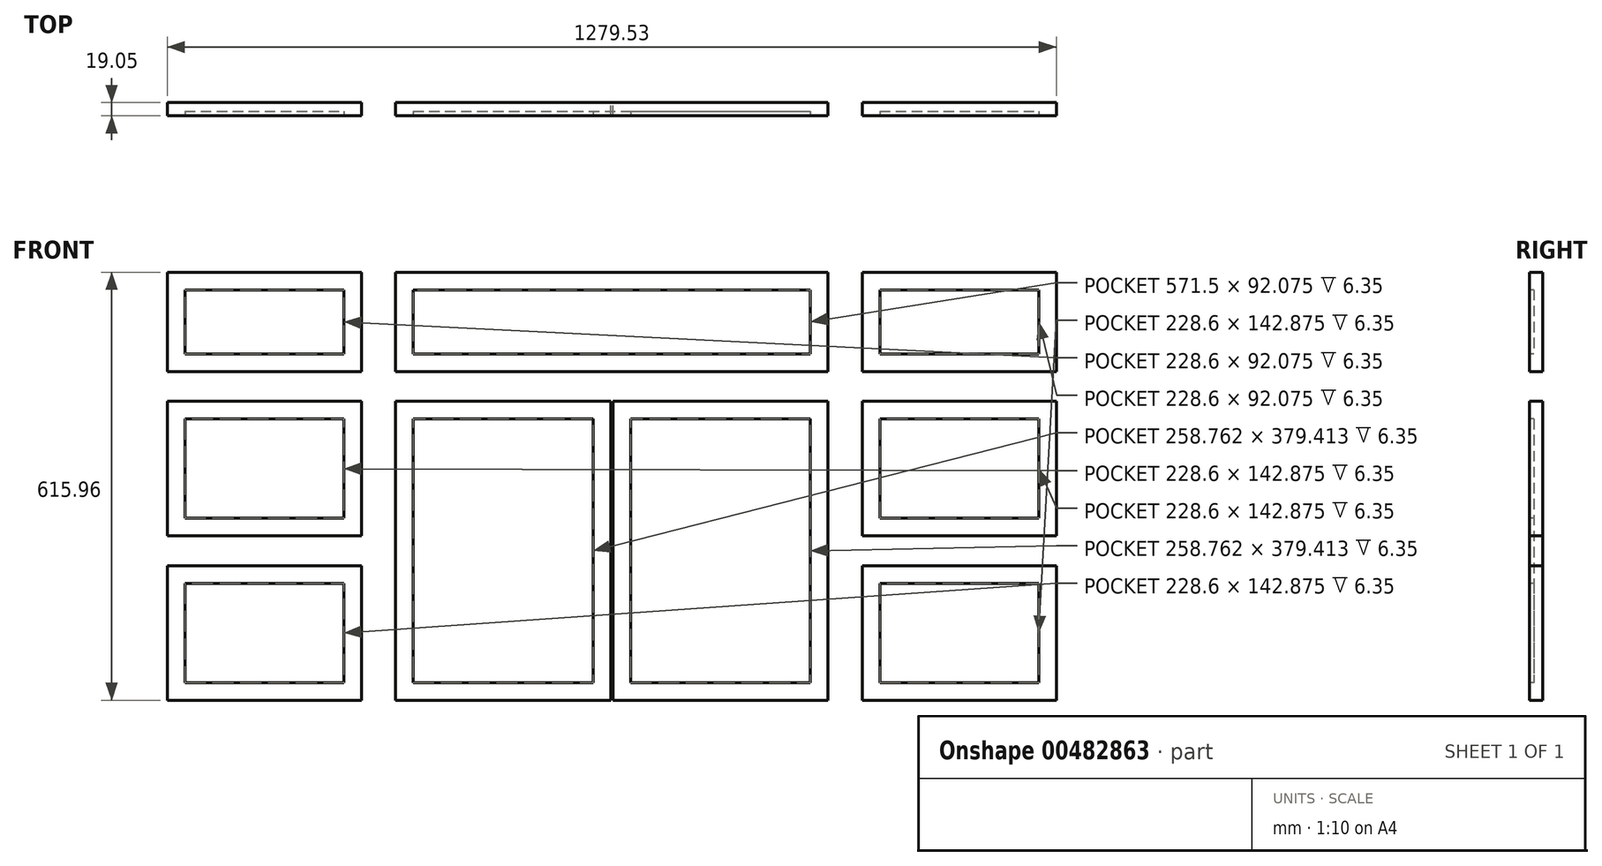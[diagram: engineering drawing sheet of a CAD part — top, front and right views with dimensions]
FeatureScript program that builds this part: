
annotation { "Feature Type Name" : "Feature", "Feature Type Description" : "" }
export const myFeature = defineFeature(function(context is Context, id is Id, definition is map)
    precondition{}
    {
        {
            var Q0;
            Q0=qCreatedBy(makeId("Front.planeOp"),FACE);
            var sketch = newSketch(context, id + "F0", { "sketchPlane" : qUnion([Q0])});
            skPoint(sketch, "E0.middle", {"position": v(0, 0) * mm});
            skLineSegment(sketch, "E1.bottom", {"start": v(-663.58, 288.92) * mm, "end": v(-384.18, 288.93) * mm});
            skLineSegment(sketch, "E1.top", {"start": v(-663.58, 146.05) * mm, "end": v(-384.18, 146.05) * mm});
            skLineSegment(sketch, "E1.left", {"start": v(-663.58, 288.92) * mm, "end": v(-663.58, 146.05) * mm});
            skLineSegment(sketch, "E1.right", {"start": v(-384.18, 288.93) * mm, "end": v(-384.18, 146.05) * mm});
            skLineSegment(sketch, "E2.bottom", {"start": v(-663.58, 103.19) * mm, "end": v(-384.18, 103.19) * mm});
            skLineSegment(sketch, "E2.top", {"start": v(-663.58, -90.49) * mm, "end": v(-384.18, -90.49) * mm});
            skLineSegment(sketch, "E2.left", {"start": v(-663.58, 103.19) * mm, "end": v(-663.58, -90.49) * mm});
            skLineSegment(sketch, "E2.right", {"start": v(-384.18, 103.19) * mm, "end": v(-384.18, -90.49) * mm});
            skLineSegment(sketch, "E3.bottom", {"start": v(-663.58, -133.35) * mm, "end": v(-384.18, -133.35) * mm});
            skLineSegment(sketch, "E3.top", {"start": v(-663.58, -327.03) * mm, "end": v(-384.18, -327.03) * mm});
            skLineSegment(sketch, "E3.left", {"start": v(-663.58, -133.35) * mm, "end": v(-663.58, -327.03) * mm});
            skLineSegment(sketch, "E3.right", {"start": v(-384.18, -133.35) * mm, "end": v(-384.18, -327.03) * mm});
            skLineSegment(sketch, "E4.bottom", {"start": v(-334.96, 288.93) * mm, "end": v(287.34, 288.93) * mm});
            skLineSegment(sketch, "E4.top", {"start": v(-334.96, 146.05) * mm, "end": v(287.34, 146.05) * mm});
            skLineSegment(sketch, "E4.left", {"start": v(-334.96, 288.93) * mm, "end": v(-334.96, 146.05) * mm});
            skLineSegment(sketch, "E4.right", {"start": v(287.34, 288.93) * mm, "end": v(287.34, 146.05) * mm});
            skLineSegment(sketch, "E5.bottom", {"start": v(336.55, 288.93) * mm, "end": v(615.95, 288.93) * mm});
            skLineSegment(sketch, "E5.top", {"start": v(336.55, 146.05) * mm, "end": v(615.95, 146.05) * mm});
            skLineSegment(sketch, "E5.left", {"start": v(336.55, 288.93) * mm, "end": v(336.55, 146.05) * mm});
            skLineSegment(sketch, "E5.right", {"start": v(615.95, 288.93) * mm, "end": v(615.95, 146.05) * mm});
            skLineSegment(sketch, "E6.bottom", {"start": v(336.55, 103.19) * mm, "end": v(615.95, 103.19) * mm});
            skLineSegment(sketch, "E6.top", {"start": v(336.55, -90.49) * mm, "end": v(615.95, -90.49) * mm});
            skLineSegment(sketch, "E6.left", {"start": v(336.55, 103.19) * mm, "end": v(336.55, -90.49) * mm});
            skLineSegment(sketch, "E6.right", {"start": v(615.95, 103.19) * mm, "end": v(615.95, -90.49) * mm});
            skLineSegment(sketch, "E7.bottom", {"start": v(336.55, -133.35) * mm, "end": v(615.95, -133.35) * mm});
            skLineSegment(sketch, "E7.top", {"start": v(336.55, -327.03) * mm, "end": v(615.95, -327.03) * mm});
            skLineSegment(sketch, "E7.left", {"start": v(336.55, -133.35) * mm, "end": v(336.55, -327.02) * mm});
            skLineSegment(sketch, "E7.right", {"start": v(615.95, -133.35) * mm, "end": v(615.95, -327.02) * mm});
            skLineSegment(sketch, "E8.bottom", {"start": v(-334.96, 103.19) * mm, "end": v(-25.4, 103.19) * mm});
            skLineSegment(sketch, "E8.top", {"start": v(-334.96, -327.03) * mm, "end": v(-25.4, -327.03) * mm});
            skLineSegment(sketch, "E8.left", {"start": v(-334.96, 103.19) * mm, "end": v(-334.96, -327.03) * mm});
            skLineSegment(sketch, "E8.right", {"start": v(-25.4, 103.19) * mm, "end": v(-25.4, -327.03) * mm});
            skLineSegment(sketch, "E9.bottom", {"start": v(-22.23, 103.19) * mm, "end": v(287.34, 103.19) * mm});
            skLineSegment(sketch, "E9.top", {"start": v(-22.23, -327.03) * mm, "end": v(287.34, -327.03) * mm});
            skLineSegment(sketch, "E9.left", {"start": v(-22.23, 103.19) * mm, "end": v(-22.23, -327.02) * mm});
            skLineSegment(sketch, "E9.right", {"start": v(287.34, 103.19) * mm, "end": v(287.34, -327.02) * mm});
            skSolve(sketch);
        }
        {
            var Q0;
            Q0=makeQuery(id+"F0.imprint","IMPRINT",FACE,{"disambiguationData":[TD([[makeQuery(id+"F0.imprint","IMPRINT",EDGE,{"derivedFrom":sQuery(id+"F0.wireOp",EDGE,"E1.bottom")}),-1.0]])]});
            var Q1;
            Q1=makeQuery(id+"F0.imprint","IMPRINT",FACE,{"disambiguationData":[TD([[makeQuery(id+"F0.imprint","IMPRINT",EDGE,{"derivedFrom":sQuery(id+"F0.wireOp",EDGE,"E4.bottom")}),-1.0]])]});
            var Q2;
            Q2=makeQuery(id+"F0.imprint","IMPRINT",FACE,{"disambiguationData":[TD([[makeQuery(id+"F0.imprint","IMPRINT",EDGE,{"derivedFrom":sQuery(id+"F0.wireOp",EDGE,"E5.bottom")}),-1.0]])]});
            var Q3;
            Q3=makeQuery(id+"F0.imprint","IMPRINT",FACE,{"disambiguationData":[TD([[makeQuery(id+"F0.imprint","IMPRINT",EDGE,{"derivedFrom":sQuery(id+"F0.wireOp",EDGE,"E6.bottom")}),-1.0]])]});
            var Q4;
            Q4=makeQuery(id+"F0.imprint","IMPRINT",FACE,{"disambiguationData":[TD([[makeQuery(id+"F0.imprint","IMPRINT",EDGE,{"derivedFrom":sQuery(id+"F0.wireOp",EDGE,"E7.bottom")}),-1.0]])]});
            var Q5;
            Q5=makeQuery(id+"F0.imprint","IMPRINT",FACE,{"disambiguationData":[TD([[makeQuery(id+"F0.imprint","IMPRINT",EDGE,{"derivedFrom":sQuery(id+"F0.wireOp",EDGE,"E9.bottom")}),-1.0]])]});
            var Q6;
            Q6=makeQuery(id+"F0.imprint","IMPRINT",FACE,{"disambiguationData":[TD([[makeQuery(id+"F0.imprint","IMPRINT",EDGE,{"derivedFrom":sQuery(id+"F0.wireOp",EDGE,"E8.bottom")}),-1.0]])]});
            var Q7;
            Q7=makeQuery(id+"F0.imprint","IMPRINT",FACE,{"disambiguationData":[TD([[makeQuery(id+"F0.imprint","IMPRINT",EDGE,{"derivedFrom":sQuery(id+"F0.wireOp",EDGE,"E2.bottom")}),-1.0]])]});
            var Q8;
            Q8=makeQuery(id+"F0.imprint","IMPRINT",FACE,{"disambiguationData":[TD([[makeQuery(id+"F0.imprint","IMPRINT",EDGE,{"derivedFrom":sQuery(id+"F0.wireOp",EDGE,"E3.bottom")}),-1.0]])]});
            extrude(context, id + "F1", {"entities" : qUnion([Q0, Q1, Q2, Q3, Q4, Q5, Q6, Q7, Q8]), "depth" : 19.05 * mm});
        }
        {
            var Q0;
            Q0=makeQuery(id+"F1.opExtrude","CAP_FACE",FACE,{"disambiguationData":[OSD([sQuery(id+"F0.wireOp",EDGE,"E2.bottom"),sQuery(id+"F0.wireOp",EDGE,"E2.top"),sQuery(id+"F0.wireOp",EDGE,"E2.left"),sQuery(id+"F0.wireOp",EDGE,"E2.right")])],"isStart":false});
            var sketch = newSketch(context, id + "F2", { "sketchPlane" : qUnion([Q0])});
            skLineSegment(sketch, "E10.bottom", {"start": v(-638.18, 263.52) * mm, "end": v(-409.57, 263.53) * mm});
            skLineSegment(sketch, "E10.top", {"start": v(-638.18, 171.45) * mm, "end": v(-409.57, 171.45) * mm});
            skLineSegment(sketch, "E10.left", {"start": v(-638.18, 263.52) * mm, "end": v(-638.18, 171.45) * mm});
            skLineSegment(sketch, "E10.right", {"start": v(-409.57, 263.53) * mm, "end": v(-409.57, 171.45) * mm});
            skLineSegment(sketch, "E11.bottom", {"start": v(-638.18, 77.79) * mm, "end": v(-409.57, 77.79) * mm});
            skLineSegment(sketch, "E11.top", {"start": v(-638.18, -65.09) * mm, "end": v(-409.57, -65.09) * mm});
            skLineSegment(sketch, "E11.left", {"start": v(-638.18, 77.79) * mm, "end": v(-638.18, -65.09) * mm});
            skLineSegment(sketch, "E11.right", {"start": v(-409.57, 77.79) * mm, "end": v(-409.57, -65.09) * mm});
            skLineSegment(sketch, "E12.bottom", {"start": v(-638.17, -158.75) * mm, "end": v(-409.57, -158.75) * mm});
            skLineSegment(sketch, "E12.top", {"start": v(-638.18, -301.63) * mm, "end": v(-409.57, -301.63) * mm});
            skLineSegment(sketch, "E12.left", {"start": v(-638.18, -158.75) * mm, "end": v(-638.18, -301.63) * mm});
            skLineSegment(sketch, "E12.right", {"start": v(-409.57, -158.75) * mm, "end": v(-409.57, -301.63) * mm});
            skLineSegment(sketch, "E13.bottom", {"start": v(-309.56, 77.79) * mm, "end": v(-50.8, 77.79) * mm});
            skLineSegment(sketch, "E13.top", {"start": v(-309.56, -301.63) * mm, "end": v(-50.8, -301.63) * mm});
            skLineSegment(sketch, "E13.left", {"start": v(-309.56, 77.79) * mm, "end": v(-309.56, -301.63) * mm});
            skLineSegment(sketch, "E13.right", {"start": v(-50.8, 77.79) * mm, "end": v(-50.8, -301.63) * mm});
            skLineSegment(sketch, "E14.bottom", {"start": v(-309.56, 263.53) * mm, "end": v(261.94, 263.53) * mm});
            skLineSegment(sketch, "E14.top", {"start": v(-309.56, 171.45) * mm, "end": v(261.94, 171.45) * mm});
            skLineSegment(sketch, "E14.left", {"start": v(-309.56, 263.53) * mm, "end": v(-309.56, 171.45) * mm});
            skLineSegment(sketch, "E14.right", {"start": v(261.94, 263.53) * mm, "end": v(261.94, 171.45) * mm});
            skLineSegment(sketch, "E15.bottom", {"start": v(3.17, 77.79) * mm, "end": v(261.94, 77.79) * mm});
            skLineSegment(sketch, "E15.top", {"start": v(3.17, -301.63) * mm, "end": v(261.94, -301.63) * mm});
            skLineSegment(sketch, "E15.left", {"start": v(3.17, 77.79) * mm, "end": v(3.17, -301.63) * mm});
            skLineSegment(sketch, "E15.right", {"start": v(261.94, 77.79) * mm, "end": v(261.94, -301.63) * mm});
            skLineSegment(sketch, "E16.bottom", {"start": v(361.95, 263.53) * mm, "end": v(590.55, 263.53) * mm});
            skLineSegment(sketch, "E16.top", {"start": v(361.95, 171.45) * mm, "end": v(590.55, 171.45) * mm});
            skLineSegment(sketch, "E16.left", {"start": v(361.95, 263.53) * mm, "end": v(361.95, 171.45) * mm});
            skLineSegment(sketch, "E16.right", {"start": v(590.55, 263.53) * mm, "end": v(590.55, 171.45) * mm});
            skLineSegment(sketch, "E17.bottom", {"start": v(361.95, 77.79) * mm, "end": v(590.55, 77.79) * mm});
            skLineSegment(sketch, "E17.top", {"start": v(361.95, -65.09) * mm, "end": v(590.55, -65.09) * mm});
            skLineSegment(sketch, "E17.left", {"start": v(361.95, 77.79) * mm, "end": v(361.95, -65.09) * mm});
            skLineSegment(sketch, "E17.right", {"start": v(590.55, 77.79) * mm, "end": v(590.55, -65.09) * mm});
            skLineSegment(sketch, "E18.bottom", {"start": v(361.95, -158.75) * mm, "end": v(590.55, -158.75) * mm});
            skLineSegment(sketch, "E18.top", {"start": v(361.95, -301.63) * mm, "end": v(590.55, -301.63) * mm});
            skLineSegment(sketch, "E18.left", {"start": v(361.95, -158.75) * mm, "end": v(361.95, -301.63) * mm});
            skLineSegment(sketch, "E18.right", {"start": v(590.55, -158.75) * mm, "end": v(590.55, -301.63) * mm});
            skSolve(sketch);
        }
        {
            var Q0;
            Q0=qSketchRegion(id+"F2",true);
            extrude(context, id + "F3", {"entities" : qUnion([Q0]), "operationType" : NewBodyOperationType.REMOVE, "oppositeDirection" : true, "depth" : 6.35 * mm});
        }
    });
